# Revit family: Windows_US-Bullet-Proofing_USAW200-1
name_source: partatom
category: Windows
units: mm (PartAtom-declared; Revit-internal decimal feet)

## family parameters
Always vertical = Yes
Cut with Voids When Loaded = No
Host = Wall
OmniClass Number = 23.30.20.00
OmniClass Title = Windows
Room Calculation Point = No
Shared = No

## types (1)
- 3' x 4'
    Assembly Code = C1010710
    Default Sill Height = 3' - 0"
    Description = USAW 200 – Operable Interior Aluminum Window
    Gap = 0' - 0 1/2"
    Glass Thickness = 0' - 1"
    Glass Thickness Note = The glazing system can be capable of accepting various thickness, ranging from ¼” to 1 3/4”
    Height = 4' - 0"
    Keynote = 08510
    Manufacturer = US Bullet Proofing
    Model = USAW 200
    Product Guid = 728d3838-c6e3-4ed3-92d0-c6df7b67fb6a
    Product data url = https://www.bimobject.com
    Product url = https://www.usbulletproofing.com
    Rough Height = 4' - 1"
    Rough Width = 3' - 1"
    URL = https://www.usbulletproofing.com
    Wall Closure = By host
    Width = 3' - 0"
    z_Glass Thickness Control = 0' - 1"
    z_Height Control = 4' - 0"
    z_Width Control = 3' - 0"

## geometry (parser evidence)
native form markers: Sweep x4
no freeform markers — native parametric forms only
